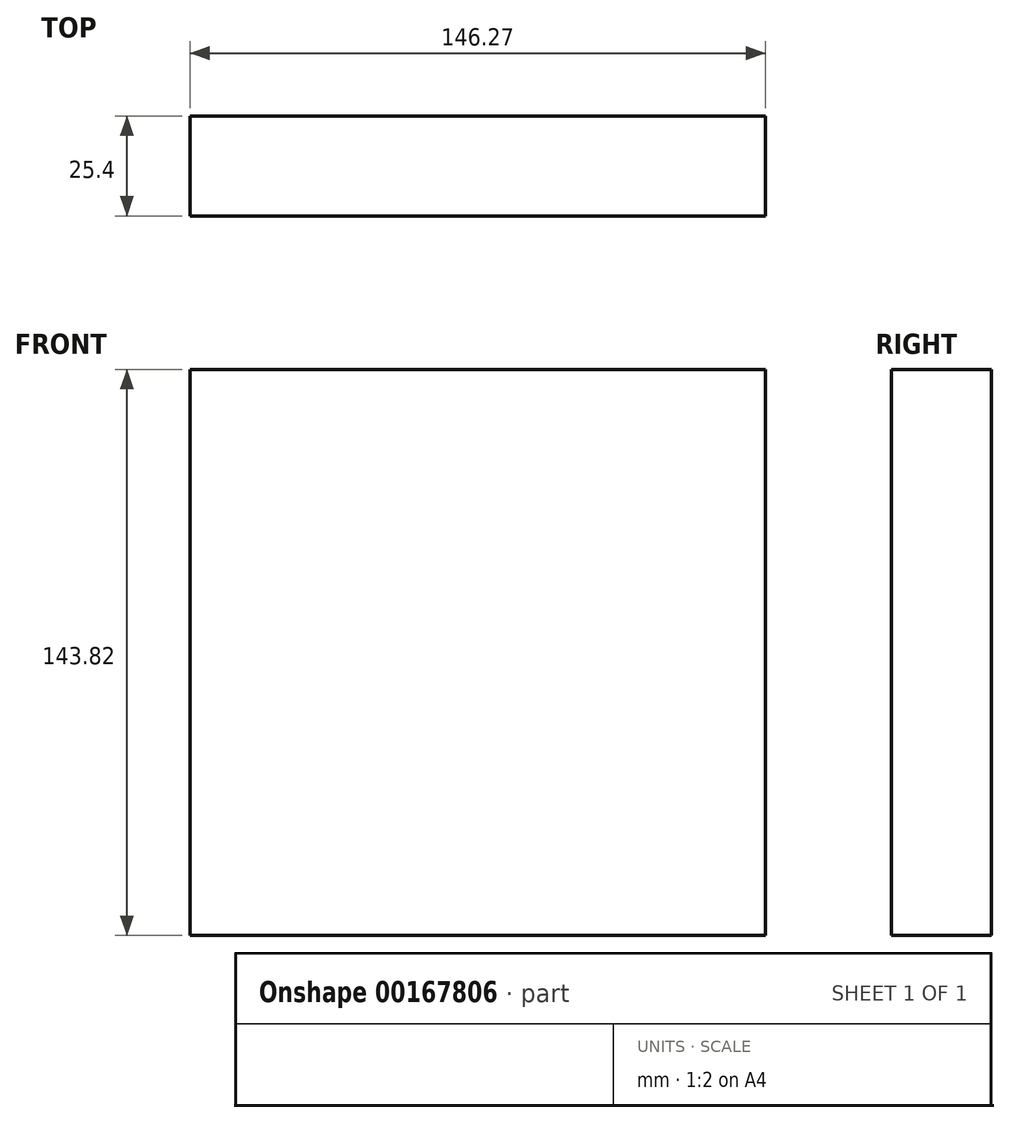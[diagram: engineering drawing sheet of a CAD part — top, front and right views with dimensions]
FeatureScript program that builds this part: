
annotation { "Feature Type Name" : "Feature", "Feature Type Description" : "" }
export const myFeature = defineFeature(function(context is Context, id is Id, definition is map)
    precondition{}
    {
        {
            var Q0;
            Q0=qCreatedBy(makeId("Front.planeOp"),FACE);
            var sketch = newSketch(context, id + "F0", { "sketchPlane" : qUnion([Q0])});
            skLineSegment(sketch, "E0.bottom", {"start": v(-75.13, 76.59) * mm, "end": v(71.14, 76.59) * mm});
            skLineSegment(sketch, "E0.top", {"start": v(-75.13, -67.23) * mm, "end": v(71.14, -67.23) * mm});
            skLineSegment(sketch, "E0.left", {"start": v(-75.13, 76.59) * mm, "end": v(-75.13, -67.23) * mm});
            skLineSegment(sketch, "E0.right", {"start": v(71.14, 76.59) * mm, "end": v(71.14, -67.23) * mm});
            skSolve(sketch);
        }
        {
            var Q0;
            Q0=makeQuery(id+"F0.imprint","IMPRINT",FACE,{"disambiguationData":[TD([[makeQuery(id+"F0.imprint","IMPRINT",EDGE,{"derivedFrom":sQuery(id+"F0.wireOp",EDGE,"E0.bottom")}),-1.0]])]});
            extrude(context, id + "F1", {"entities" : qUnion([Q0]), "depth" : 25.4 * mm});
        }
    });
